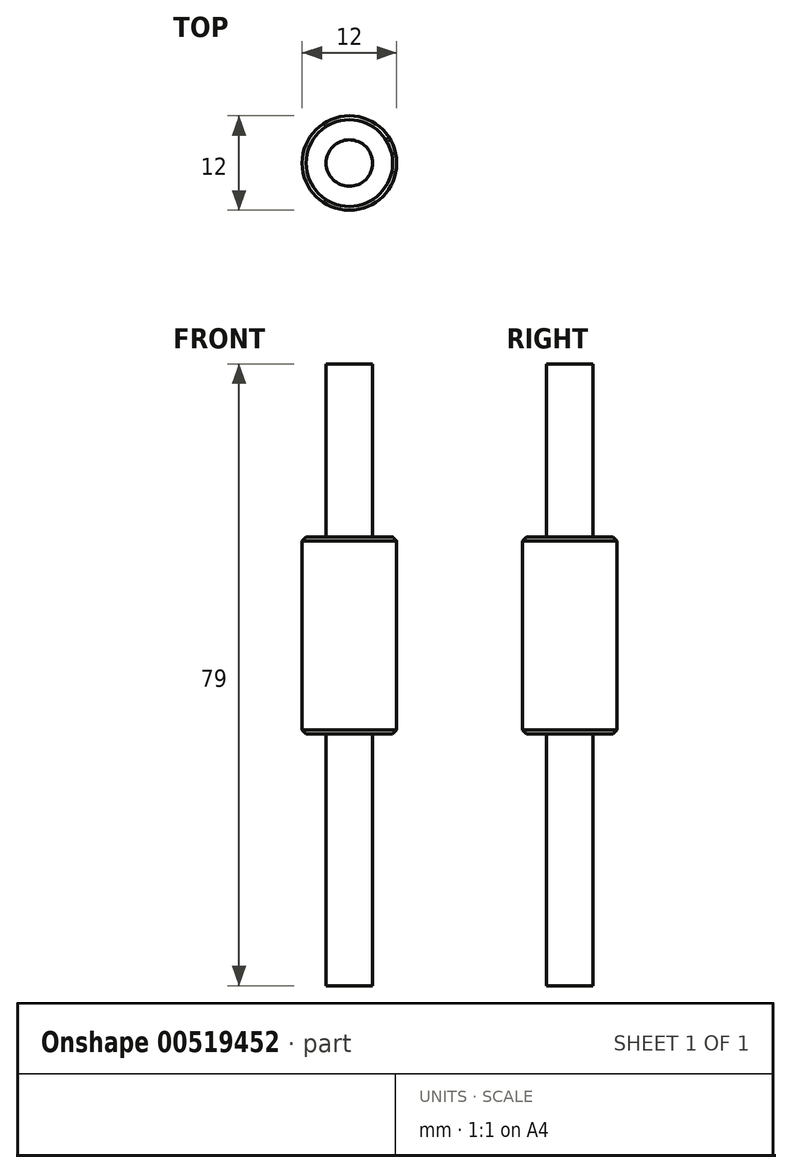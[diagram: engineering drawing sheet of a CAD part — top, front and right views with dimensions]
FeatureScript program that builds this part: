
annotation { "Feature Type Name" : "Feature", "Feature Type Description" : "" }
export const myFeature = defineFeature(function(context is Context, id is Id, definition is map)
    precondition{}
    {
        {
            var Q0;
            Q0=qCreatedBy(makeId("Top.planeOp"),FACE);
            var sketch = newSketch(context, id + "F0", { "sketchPlane" : qUnion([Q0])});
            skCircle(sketch, "E0", {"center": v(0, 0) * mm, "radius": 2.95 * mm});
            skCircle(sketch, "E1", {"center": v(0, 0) * mm, "radius": 6 * mm});
            skSolve(sketch);
        }
        {
            var Q0;
            Q0=qCreatedBy(makeId("Top.planeOp"),FACE);
            cPlane(context, id + "F1", {"entities" : qUnion([Q0]), "cplaneType" : CPlaneType.OFFSET, "offset" : 25 * mm, "width" : 150 * mm, "height" : 150 * mm});
        }
        {
            var Q0;
            Q0=qCreatedBy(id+"F1.planeOp",FACE);
            var sketch = newSketch(context, id + "F2", { "sketchPlane" : qUnion([Q0])});
            skCircle(sketch, "E2.0", {"center": v(0, 0) * mm, "radius": 2.95 * mm});
            skSolve(sketch);
        }
        {
            var Q0;
            Q0=makeQuery(id+"F0.imprint","IMPRINT",FACE,{"disambiguationData":[TD([[makeQuery(id+"F0.imprint","IMPRINT",EDGE,{"derivedFrom":sQuery(id+"F0.wireOp",EDGE,"E0")}),1.0]])]});
            extrude(context, id + "F3", {"entities" : qUnion([Q0]), "oppositeDirection" : true, "depth" : 32 * mm, "offsetDistance" : 25 * mm});
        }
        {
            var Q0;
            Q0=makeQuery(id+"F0.imprint","IMPRINT",FACE,{"disambiguationData":[TD([[makeQuery(id+"F0.imprint","IMPRINT",EDGE,{"derivedFrom":sQuery(id+"F0.wireOp",EDGE,"E0")}),1.0]])]});
            var Q1;
            Q1=makeQuery(id+"F0.imprint","IMPRINT",FACE,{"disambiguationData":[TD([[makeQuery(id+"F0.imprint","IMPRINT",EDGE,{"derivedFrom":sQuery(id+"F0.wireOp",EDGE,"E0")}),-1.0]])]});
            extrude(context, id + "F4", {"entities" : qUnion([Q0, Q1]), "operationType" : NewBodyOperationType.ADD, "depth" : 25 * mm, "offsetDistance" : 25 * mm});
        }
        {
            var Q0;
            Q0=makeQuery(id+"F2.imprint","IMPRINT",FACE,{"disambiguationData":[TD([[makeQuery(id+"F2.imprint","IMPRINT",EDGE,{"derivedFrom":sQuery(id+"F2.wireOp",EDGE,"E2.0")}),1.0]])]});
            extrude(context, id + "F5", {"entities" : qUnion([Q0]), "operationType" : NewBodyOperationType.ADD, "depth" : 22 * mm, "offsetDistance" : 25 * mm});
        }
        {
            var Q0;
            Q0=makeQuery(id+"F4.opExtrude","CAP_EDGE",EDGE,{"disambiguationData":[OSD([sQuery(id+"F0.wireOp",EDGE,"E1")])],"isStart":false});
            var Q1;
            Q1=makeQuery(id+"F4.opExtrude","CAP_EDGE",EDGE,{"disambiguationData":[OSD([sQuery(id+"F0.wireOp",EDGE,"E1")])],"isStart":true});
            chamfer(context, id + "F6", {"entities" : qUnion([Q0, Q1]), "width" : .5 * mm, "tangentPropagation" : true});
        }
    });
